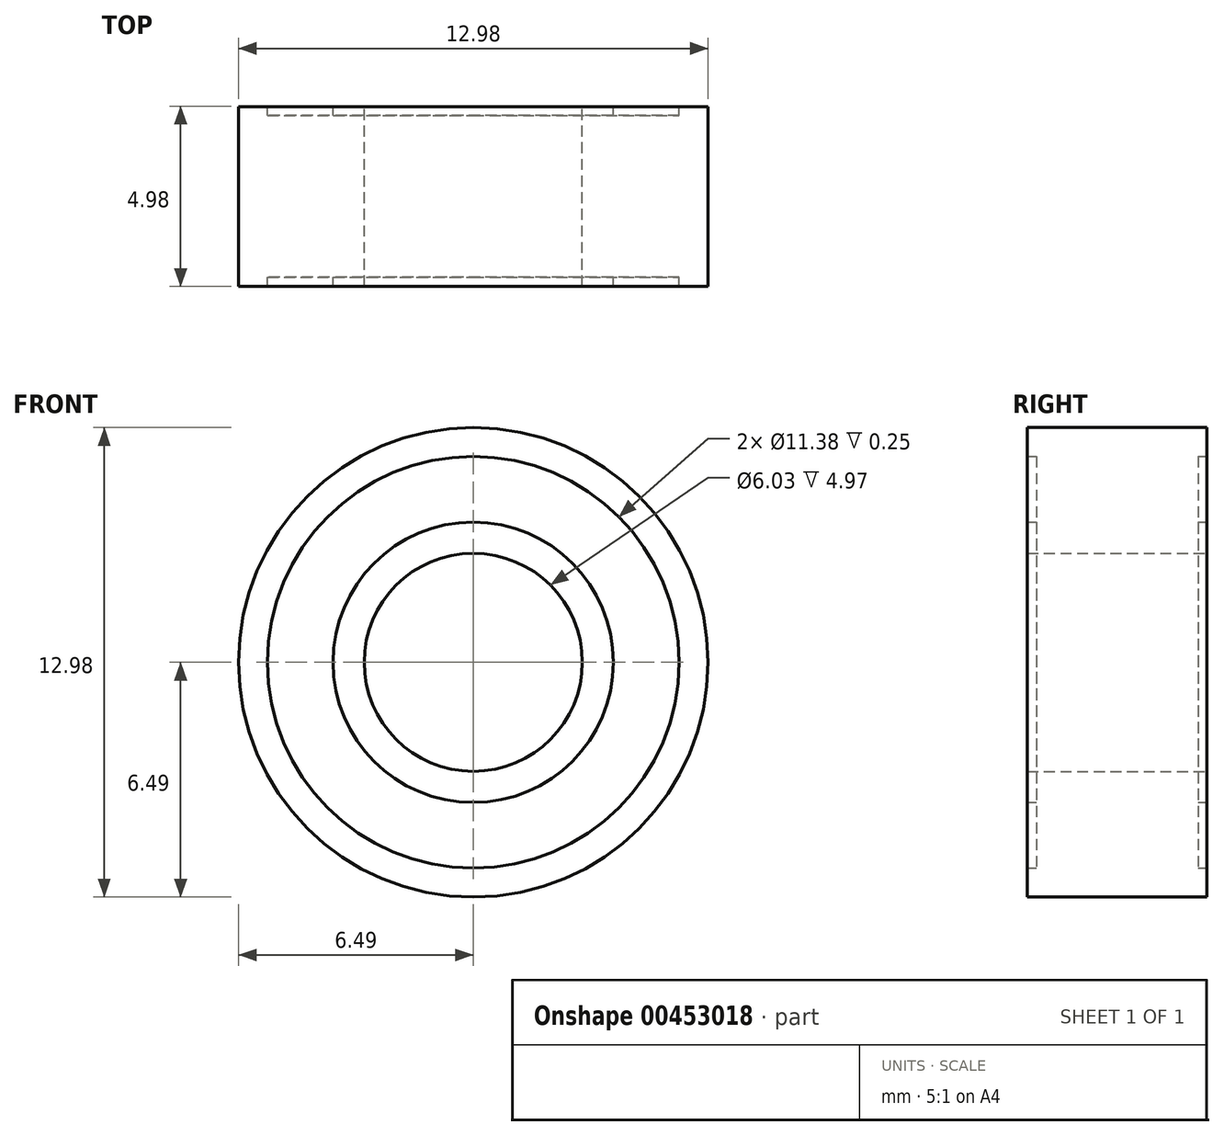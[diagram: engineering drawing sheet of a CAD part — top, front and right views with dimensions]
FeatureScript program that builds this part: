
annotation { "Feature Type Name" : "Feature", "Feature Type Description" : "" }
export const myFeature = defineFeature(function(context is Context, id is Id, definition is map)
    precondition{}
    {
        {
            var Q0;
            Q0=qCreatedBy(makeId("Top.planeOp"),FACE);
            var sketch = newSketch(context, id + "F0", { "sketchPlane" : qUnion([Q0])});
            skLineSegment(sketch, "E0", {"start": v(-6.49, 0) * mm, "end": v(-6.49, 2.48) * mm});
            skLineSegment(sketch, "E1", {"start": v(-6.49, 2.48) * mm, "end": v(-5.69, 2.48) * mm});
            skLineSegment(sketch, "E2", {"start": v(-5.69, 2.48) * mm, "end": v(-5.69, 0) * mm});
            skLineSegment(sketch, "E3", {"start": v(-5.69, 2.23) * mm, "end": v(-3.87, 2.23) * mm});
            skLineSegment(sketch, "E4", {"start": v(-3.87, 2.48) * mm, "end": v(-3.87, 0) * mm});
            skLineSegment(sketch, "E5", {"start": v(-3.87, 2.48) * mm, "end": v(-3.01, 2.48) * mm});
            skLineSegment(sketch, "E6", {"start": v(-3.01, 2.48) * mm, "end": v(-3.01, 0) * mm});
            skLineSegment(sketch, "E7", {"start": v(0, 10.7) * mm, "end": v(0, -5.1) * mm, "construction": true});
            skLineSegment(sketch, "E8", {"start": v(-6.5, 0) * mm, "end": v(-3.02, 0) * mm, "construction": true});
            skLineSegment(sketch, "E9.MirrorCS", {"start": v(-3.87, -2.48) * mm, "end": v(-3.87, 0) * mm});
            skLineSegment(sketch, "E10.MirrorCS", {"start": v(-3.01, -2.48) * mm, "end": v(-3.01, 0) * mm});
            skLineSegment(sketch, "E11.MirrorCS", {"start": v(-3.87, -2.48) * mm, "end": v(-3.01, -2.48) * mm});
            skLineSegment(sketch, "E12.MirrorCS", {"start": v(-5.69, -2.23) * mm, "end": v(-3.87, -2.23) * mm});
            skLineSegment(sketch, "E13.MirrorCS", {"start": v(-5.69, -2.48) * mm, "end": v(-5.69, 0) * mm});
            skLineSegment(sketch, "E14.MirrorCS", {"start": v(-6.49, -2.48) * mm, "end": v(-5.69, -2.48) * mm});
            skLineSegment(sketch, "E15.MirrorCS", {"start": v(-6.49, 0) * mm, "end": v(-6.49, -2.48) * mm});
            skSolve(sketch);
        }
        {
            var Q0;
            Q0=makeQuery(id+"F0.imprint","IMPRINT",FACE,{"disambiguationData":[TD([[makeQuery(id+"F0.imprint","IMPRINT",EDGE,{"derivedFrom":sQuery(id+"F0.wireOp",EDGE,"E0")}),-1.0]])]});
            var Q1;
            {var subQ1=sQuery(id+"F0.wireOp",EDGE,"E3");Q1=makeQuery(id+"F0.imprint","IMPRINT",FACE,{"disambiguationData":[TD([[makeQuery(id+"F0.imprint","IMPRINT",EDGE,{"derivedFrom":subQ1}),-1.0]])]});}
            var Q2;
            {var subQ0=sQuery(id+"F0.wireOp",EDGE,"E5");Q2=makeQuery(id+"F0.imprint","IMPRINT",FACE,{"disambiguationData":[TD([[makeQuery(id+"F0.imprint","IMPRINT",EDGE,{"derivedFrom":subQ0}),-1.0]])]});}
            var Q3;
            Q3=sQuery(id+"F0.wireOp",EDGE,"E7");
            revolve(context, id + "F1", {"surfaceOperationType" : NewSurfaceOperationType.NEW, "entities" : qUnion([Q0, Q1, Q2]), "axis" : qUnion([Q3]), "revolveType" : RevolveType.FULL});
        }
    });
